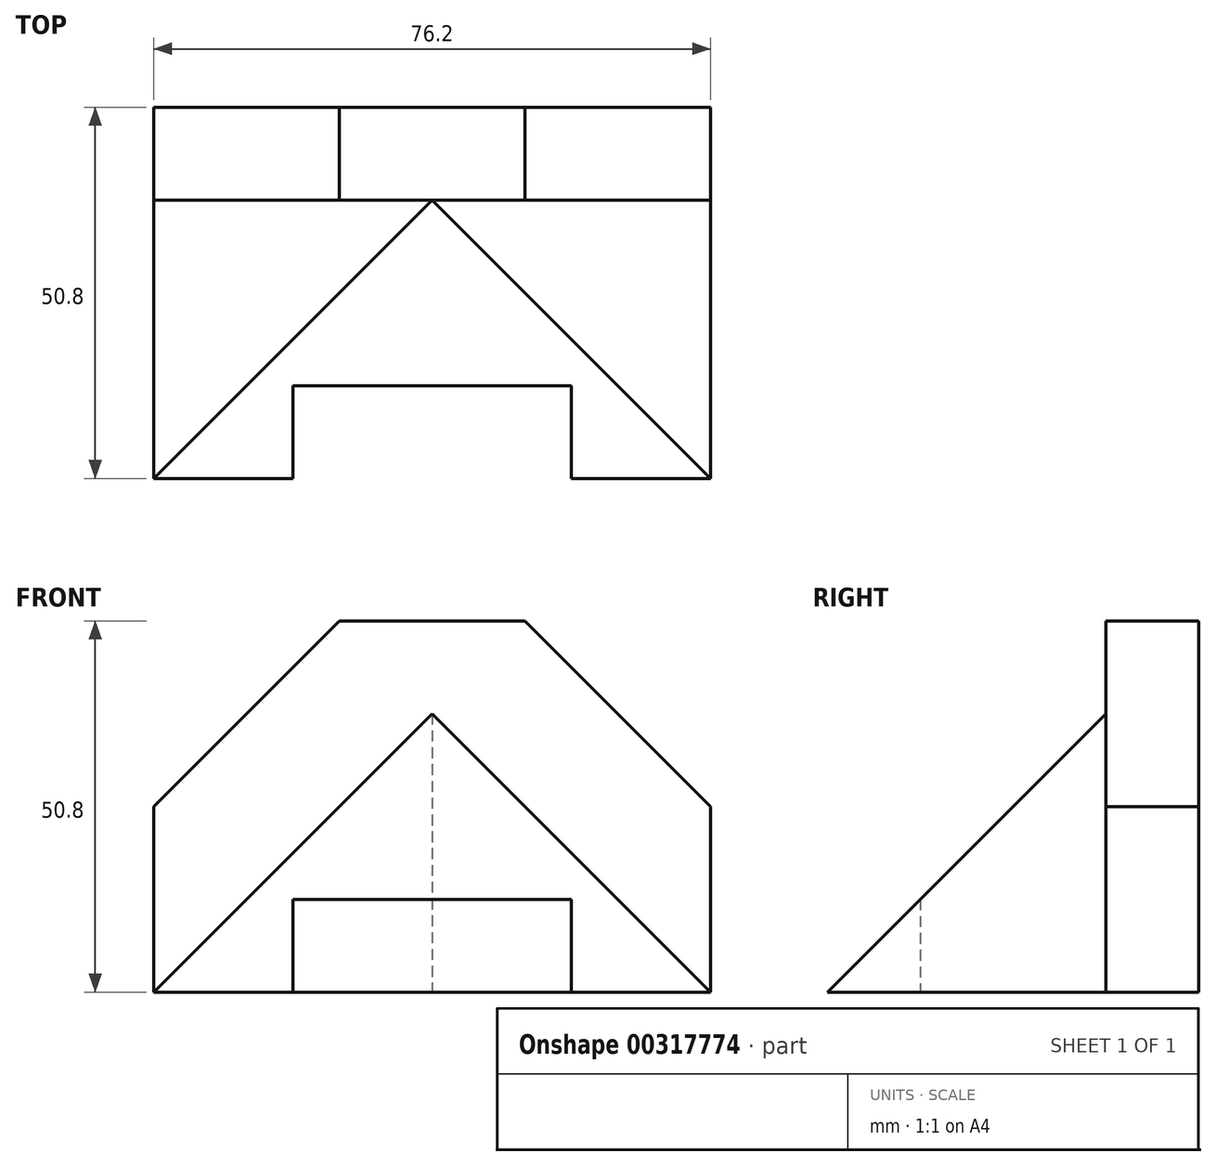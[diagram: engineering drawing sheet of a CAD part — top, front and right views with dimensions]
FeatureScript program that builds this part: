
annotation { "Feature Type Name" : "Feature", "Feature Type Description" : "" }
export const myFeature = defineFeature(function(context is Context, id is Id, definition is map)
    precondition{}
    {
        {
            var Q0;
            Q0=qCreatedBy(makeId("Front.planeOp"),FACE);
            var sketch = newSketch(context, id + "F0", { "sketchPlane" : qUnion([Q0])});
            skLineSegment(sketch, "E0", {"start": v(0, 0) * mm, "end": v(0, 25.4) * mm});
            skLineSegment(sketch, "E1", {"start": v(0, 25.4) * mm, "end": v(25.4, 50.8) * mm});
            skLineSegment(sketch, "E2", {"start": v(25.4, 50.8) * mm, "end": v(50.8, 50.8) * mm});
            skLineSegment(sketch, "E3", {"start": v(50.8, 50.8) * mm, "end": v(76.2, 25.4) * mm});
            skLineSegment(sketch, "E4", {"start": v(76.2, 25.4) * mm, "end": v(76.2, 0) * mm});
            skLineSegment(sketch, "E5", {"start": v(76.2, 0) * mm, "end": v(0, 0) * mm});
            skSolve(sketch);
        }
        {
            var Q0;
            Q0=makeQuery(id+"F0.imprint","IMPRINT",FACE,{"disambiguationData":[TD([[makeQuery(id+"F0.imprint","IMPRINT",EDGE,{"derivedFrom":sQuery(id+"F0.wireOp",EDGE,"E0")}),-1.0]])]});
            extrude(context, id + "F1", {"entities" : qUnion([Q0]), "depth" : 12.7 * mm});
        }
        {
            var Q0;
            Q0=qCreatedBy(makeId("Top.planeOp"),FACE);
            var sketch = newSketch(context, id + "F2", { "sketchPlane" : qUnion([Q0])});
            skLineSegment(sketch, "E6", {"start": v(0, -50.8) * mm, "end": v(38.1, -12.7) * mm});
            skLineSegment(sketch, "E7", {"start": v(38.1, -12.7) * mm, "end": v(76.2, -50.8) * mm});
            skLineSegment(sketch, "E8", {"start": v(76.2, -50.8) * mm, "end": v(57.15, -50.8) * mm});
            skLineSegment(sketch, "E9", {"start": v(57.15, -50.8) * mm, "end": v(57.15, -38.1) * mm});
            skLineSegment(sketch, "E10", {"start": v(57.15, -38.1) * mm, "end": v(19.05, -38.1) * mm});
            skLineSegment(sketch, "E11", {"start": v(19.05, -38.1) * mm, "end": v(19.05, -50.8) * mm});
            skLineSegment(sketch, "E12", {"start": v(19.05, -50.8) * mm, "end": v(0, -50.8) * mm});
            skSolve(sketch);
        }
        {
            var Q0;
            Q0 = qSketchRegion(id + "F2", true);
            extrude(context, id + "F3", {"entities" : qUnion([Q0]), "depth" : 38.1 * mm});
        }
        {
            var Q0;
            Q0=makeQuery(id+"F1.opExtrude","SWEPT_FACE",FACE,{"disambiguationData":[OSD([sQuery(id+"F0.wireOp",EDGE,"E4")])]});
            var sketch = newSketch(context, id + "F4", { "sketchPlane" : qUnion([Q0])});
            skLineSegment(sketch, "E13", {"start": v(-50.8, 0) * mm, "end": v(-12.7, 38.1) * mm});
            skLineSegment(sketch, "E14", {"start": v(-12.7, 38.1) * mm, "end": v(-50.8, 38.1) * mm});
            skLineSegment(sketch, "E15", {"start": v(-50.8, 38.1) * mm, "end": v(-50.8, 0) * mm});
            skSolve(sketch);
        }
        {
            var Q0;
            Q0 = qSketchRegion(id + "F4", true);
            extrude(context, id + "F5", {"entities" : qUnion([Q0]), "operationType" : NewBodyOperationType.REMOVE, "endBound" : BoundingType.THROUGH_ALL, "oppositeDirection" : true, "depth" : 25.4 * mm});
        }
        {
            var Q0;
            Q0=qCreatedBy(makeId("Top.planeOp"),FACE);
            var sketch = newSketch(context, id + "F6", { "sketchPlane" : qUnion([Q0])});
            skLineSegment(sketch, "E16", {"start": v(0, -12.7) * mm, "end": v(0, -50.8) * mm});
            skLineSegment(sketch, "E17", {"start": v(0, -50.8) * mm, "end": v(38.1, -12.7) * mm});
            skLineSegment(sketch, "E18", {"start": v(38.1, -12.7) * mm, "end": v(0, -12.7) * mm});
            skLineSegment(sketch, "E19", {"start": v(38.1, -12.7) * mm, "end": v(76.2, -50.8) * mm});
            skLineSegment(sketch, "E20", {"start": v(76.2, -50.8) * mm, "end": v(76.2, -12.7) * mm});
            skLineSegment(sketch, "E21", {"start": v(76.2, -12.7) * mm, "end": v(38.1, -12.7) * mm});
            skSolve(sketch);
        }
        {
            var Q0;
            Q0 = qSketchRegion(id + "F6", true);
            extrude(context, id + "F7", {"entities" : qUnion([Q0]), "depth" : 38.1 * mm});
        }
        {
            var Q0;
            Q0=makeQuery(id+"F3.opExtrude","SWEPT_FACE",FACE,{"disambiguationData":[OSD([sQuery(id+"F2.wireOp",EDGE,"E10")])]});
            var sketch = newSketch(context, id + "F8", { "sketchPlane" : qUnion([Q0])});
            skLineSegment(sketch, "E22", {"start": v(38.1, 38.1) * mm, "end": v(76.2, 0) * mm});
            skLineSegment(sketch, "E23", {"start": v(76.2, 0) * mm, "end": v(76.2, 38.1) * mm});
            skLineSegment(sketch, "E24", {"start": v(76.2, 38.1) * mm, "end": v(38.1, 38.1) * mm});
            skLineSegment(sketch, "E25", {"start": v(38.1, 38.1) * mm, "end": v(0, 0) * mm});
            skLineSegment(sketch, "E26", {"start": v(0, 0) * mm, "end": v(0, 38.1) * mm});
            skLineSegment(sketch, "E27", {"start": v(0, 38.1) * mm, "end": v(38.1, 38.1) * mm});
            skSolve(sketch);
        }
        {
            var Q0;
            Q0=makeQuery(id+"F8.imprint","IMPRINT",FACE,{"disambiguationData":[TD([[makeQuery(id+"F8.imprint","IMPRINT",EDGE,{"derivedFrom":sQuery(id+"F8.wireOp",EDGE,"E25")}),-1.0]])]});
            extrude(context, id + "F9", {"entities" : qUnion([Q0]), "operationType" : NewBodyOperationType.REMOVE, "oppositeDirection" : true, "depth" : 25.4 * mm, "hasSecondDirection" : true, "secondDirectionOppositeDirection" : false, "secondDirectionDepth" : 25.4 * mm});
        }
        {
            var Q0;
            Q0=makeQuery(id+"F8.imprint","IMPRINT",FACE,{"disambiguationData":[TD([[makeQuery(id+"F8.imprint","IMPRINT",EDGE,{"derivedFrom":sQuery(id+"F8.wireOp",EDGE,"E22")}),1.0]])]});
            extrude(context, id + "F10", {"entities" : qUnion([Q0]), "operationType" : NewBodyOperationType.REMOVE, "oppositeDirection" : true, "depth" : 25.4 * mm, "hasSecondDirection" : true, "secondDirectionOppositeDirection" : false, "secondDirectionDepth" : 25.4 * mm});
        }
    });
